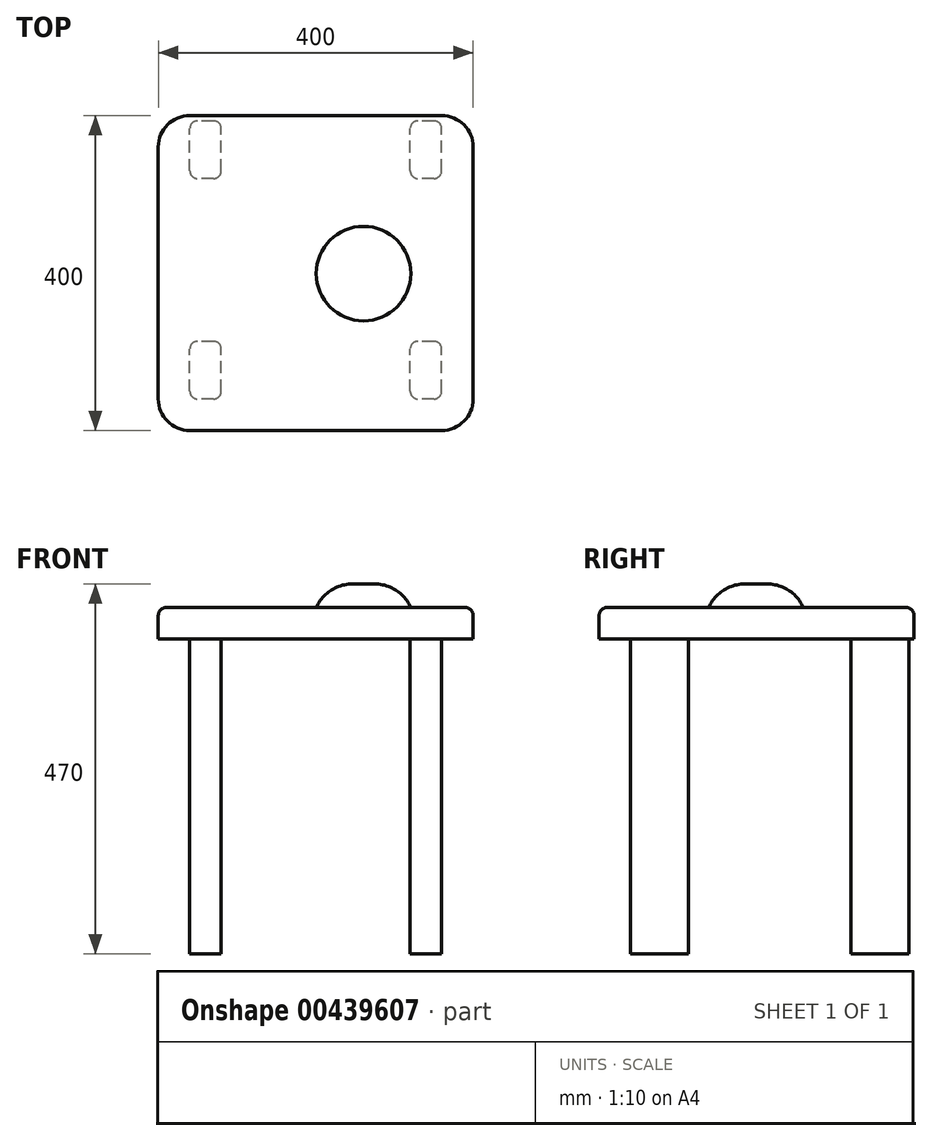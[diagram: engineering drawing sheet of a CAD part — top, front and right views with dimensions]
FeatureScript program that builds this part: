
annotation { "Feature Type Name" : "Feature", "Feature Type Description" : "" }
export const myFeature = defineFeature(function(context is Context, id is Id, definition is map)
    precondition{}
    {
        {
            var Q0;
            Q0=qCreatedBy(makeId("Top.planeOp"),FACE);
            var sketch = newSketch(context, id + "F0", { "sketchPlane" : qUnion([Q0])});
            skLineSegment(sketch, "E0.bottom", {"start": v(-220.7, -199.26) * mm, "end": v(99.3, -199.26) * mm});
            skLineSegment(sketch, "E0.top", {"start": v(-220.7, 200.74) * mm, "end": v(99.3, 200.74) * mm});
            skLineSegment(sketch, "E0.left", {"start": v(-260.7, -159.26) * mm, "end": v(-260.7, 160.74) * mm});
            skLineSegment(sketch, "E0.right", {"start": v(139.3, -159.26) * mm, "end": v(139.3, 160.74) * mm});
            skPoint(sketch, "E1.visualSharp", {"position": v(-260.7, 200.74) * mm});
            skArc(sketch, "E1.filletArc", {"start": v(-220.7, 200.74) * mm, "mid": v(-248.99, 189.03) * mm, "end": v(-260.7, 160.74) * mm});
            skPoint(sketch, "E2.visualSharp", {"position": v(139.3, 200.74) * mm});
            skArc(sketch, "E2.filletArc", {"start": v(139.3, 160.74) * mm, "mid": v(127.58, 189.03) * mm, "end": v(99.3, 200.74) * mm});
            skPoint(sketch, "E3.visualSharp", {"position": v(139.3, -199.26) * mm});
            skArc(sketch, "E3.filletArc", {"start": v(99.3, -199.26) * mm, "mid": v(127.58, -187.54) * mm, "end": v(139.3, -159.26) * mm});
            skPoint(sketch, "E4.visualSharp", {"position": v(-260.7, -199.26) * mm});
            skArc(sketch, "E4.filletArc", {"start": v(-260.7, -159.26) * mm, "mid": v(-248.99, -187.54) * mm, "end": v(-220.7, -199.26) * mm});
            skSolve(sketch);
        }
        {
            var Q0;
            Q0 = qSketchRegion(id + "F0", true);
            extrude(context, id + "F1", {"entities" : qUnion([Q0]), "depth" : 40 * mm});
        }
        {
            var Q0;
            Q0=makeQuery(id+"F1.opExtrude","CAP_FACE",FACE,{"disambiguationData":[OSD([sQuery(id+"F0.wireOp",EDGE,"E0.bottom"),sQuery(id+"F0.wireOp",EDGE,"E0.top"),sQuery(id+"F0.wireOp",EDGE,"E0.left"),sQuery(id+"F0.wireOp",EDGE,"E0.right"),sQuery(id+"F0.wireOp",EDGE,"E1.filletArc"),sQuery(id+"F0.wireOp",EDGE,"E2.filletArc"),sQuery(id+"F0.wireOp",EDGE,"E3.filletArc"),sQuery(id+"F0.wireOp",EDGE,"E4.filletArc")])],"isStart":false});
            fillet(context, id + "F2", {"entities" : qUnion([Q0]), "radius" : 10 * mm, "tangentPropagation" : true, "allowEdgeOverflow" : false});
        }
        {
            var Q0;
            Q0=makeQuery(id+"F1.opExtrude","CAP_FACE",FACE,{"disambiguationData":[OSD([sQuery(id+"F0.wireOp",EDGE,"E0.bottom"),sQuery(id+"F0.wireOp",EDGE,"E0.top"),sQuery(id+"F0.wireOp",EDGE,"E0.left"),sQuery(id+"F0.wireOp",EDGE,"E0.right"),sQuery(id+"F0.wireOp",EDGE,"E1.filletArc"),sQuery(id+"F0.wireOp",EDGE,"E2.filletArc"),sQuery(id+"F0.wireOp",EDGE,"E3.filletArc"),sQuery(id+"F0.wireOp",EDGE,"E4.filletArc")])],"isStart":true});
            var sketch = newSketch(context, id + "F3", { "sketchPlane" : qUnion([Q0])});
            skLineSegment(sketch, "E5.bottom", {"start": v(89.3, 159.26) * mm, "end": v(69.3, 159.26) * mm});
            skLineSegment(sketch, "E5.top", {"start": v(89.3, 86) * mm, "end": v(69.3, 86) * mm});
            skLineSegment(sketch, "E5.left", {"start": v(99.3, 149.26) * mm, "end": v(99.3, 96) * mm});
            skLineSegment(sketch, "E5.right", {"start": v(59.3, 149.26) * mm, "end": v(59.3, 96) * mm});
            skPoint(sketch, "E6.visualSharp", {"position": v(99.3, 159.26) * mm});
            skArc(sketch, "E6.filletArc", {"start": v(99.3, 149.26) * mm, "mid": v(96.37, 156.33) * mm, "end": v(89.3, 159.26) * mm});
            skPoint(sketch, "E7.visualSharp", {"position": v(99.3, 86) * mm});
            skArc(sketch, "E7.filletArc", {"start": v(89.3, 86) * mm, "mid": v(96.37, 88.93) * mm, "end": v(99.3, 96) * mm});
            skPoint(sketch, "E8.visualSharp", {"position": v(59.3, 86) * mm});
            skArc(sketch, "E8.filletArc", {"start": v(59.3, 96) * mm, "mid": v(62.22, 88.93) * mm, "end": v(69.3, 86) * mm});
            skPoint(sketch, "E9.visualSharp", {"position": v(59.3, 159.26) * mm});
            skArc(sketch, "E9.filletArc", {"start": v(69.3, 159.26) * mm, "mid": v(62.22, 156.33) * mm, "end": v(59.3, 149.26) * mm});
            skPoint(sketch, "E10.0.1.0", {"position": v(99.3, -194) * mm});
            skPoint(sketch, "E10.0.1.1", {"position": v(59.3, -120.74) * mm});
            skLineSegment(sketch, "E10.0.1.2", {"start": v(99.3, -130.74) * mm, "end": v(99.3, -184) * mm});
            skPoint(sketch, "E10.0.1.3", {"position": v(99.3, -120.74) * mm});
            skLineSegment(sketch, "E10.0.1.4", {"start": v(89.3, -194) * mm, "end": v(69.3, -194) * mm});
            skPoint(sketch, "E10.0.1.5", {"position": v(59.3, -194) * mm});
            skLineSegment(sketch, "E10.0.1.6", {"start": v(59.3, -130.74) * mm, "end": v(59.3, -184) * mm});
            skArc(sketch, "E10.0.1.7", {"start": v(59.3, -184) * mm, "mid": v(62.22, -191.07) * mm, "end": v(69.3, -194) * mm});
            skArc(sketch, "E10.0.1.8", {"start": v(69.3, -120.74) * mm, "mid": v(62.22, -123.67) * mm, "end": v(59.3, -130.74) * mm});
            skArc(sketch, "E10.0.1.9", {"start": v(99.3, -130.74) * mm, "mid": v(96.37, -123.67) * mm, "end": v(89.3, -120.74) * mm});
            skArc(sketch, "E10.0.1.10", {"start": v(89.3, -194) * mm, "mid": v(96.37, -191.07) * mm, "end": v(99.3, -184) * mm});
            skLineSegment(sketch, "E10.0.1.11", {"start": v(89.3, -120.74) * mm, "end": v(69.3, -120.74) * mm});
            skPoint(sketch, "E10.1.0.0", {"position": v(-180.7, 86) * mm});
            skPoint(sketch, "E10.1.0.1", {"position": v(-220.7, 159.26) * mm});
            skLineSegment(sketch, "E10.1.0.2", {"start": v(-180.7, 149.26) * mm, "end": v(-180.7, 96) * mm});
            skPoint(sketch, "E10.1.0.3", {"position": v(-180.7, 159.26) * mm});
            skLineSegment(sketch, "E10.1.0.4", {"start": v(-190.7, 86) * mm, "end": v(-210.7, 86) * mm});
            skPoint(sketch, "E10.1.0.5", {"position": v(-220.7, 86) * mm});
            skLineSegment(sketch, "E10.1.0.6", {"start": v(-220.7, 149.26) * mm, "end": v(-220.7, 96) * mm});
            skArc(sketch, "E10.1.0.7", {"start": v(-220.7, 96) * mm, "mid": v(-217.78, 88.93) * mm, "end": v(-210.7, 86) * mm});
            skArc(sketch, "E10.1.0.8", {"start": v(-210.7, 159.26) * mm, "mid": v(-217.78, 156.33) * mm, "end": v(-220.7, 149.26) * mm});
            skArc(sketch, "E10.1.0.9", {"start": v(-180.7, 149.26) * mm, "mid": v(-183.63, 156.33) * mm, "end": v(-190.7, 159.26) * mm});
            skArc(sketch, "E10.1.0.10", {"start": v(-190.7, 86) * mm, "mid": v(-183.63, 88.93) * mm, "end": v(-180.7, 96) * mm});
            skLineSegment(sketch, "E10.1.0.11", {"start": v(-190.7, 159.26) * mm, "end": v(-210.7, 159.26) * mm});
            skPoint(sketch, "E10.1.1.0", {"position": v(-180.7, -194) * mm});
            skPoint(sketch, "E10.1.1.1", {"position": v(-220.7, -120.74) * mm});
            skLineSegment(sketch, "E10.1.1.2", {"start": v(-180.7, -130.74) * mm, "end": v(-180.7, -184) * mm});
            skPoint(sketch, "E10.1.1.3", {"position": v(-180.7, -120.74) * mm});
            skLineSegment(sketch, "E10.1.1.4", {"start": v(-190.7, -194) * mm, "end": v(-210.7, -194) * mm});
            skPoint(sketch, "E10.1.1.5", {"position": v(-220.7, -194) * mm});
            skLineSegment(sketch, "E10.1.1.6", {"start": v(-220.7, -130.74) * mm, "end": v(-220.7, -184) * mm});
            skArc(sketch, "E10.1.1.7", {"start": v(-220.7, -184) * mm, "mid": v(-217.78, -191.07) * mm, "end": v(-210.7, -194) * mm});
            skArc(sketch, "E10.1.1.8", {"start": v(-210.7, -120.74) * mm, "mid": v(-217.78, -123.67) * mm, "end": v(-220.7, -130.74) * mm});
            skArc(sketch, "E10.1.1.9", {"start": v(-180.7, -130.74) * mm, "mid": v(-183.63, -123.67) * mm, "end": v(-190.7, -120.74) * mm});
            skArc(sketch, "E10.1.1.10", {"start": v(-190.7, -194) * mm, "mid": v(-183.63, -191.07) * mm, "end": v(-180.7, -184) * mm});
            skLineSegment(sketch, "E10.1.1.11", {"start": v(-190.7, -120.74) * mm, "end": v(-210.7, -120.74) * mm});
            skLineSegment(sketch, "E10.direction1", {"start": v(59.3, 86) * mm, "end": v(-220.7, 86) * mm, "construction": true});
            skLineSegment(sketch, "E10.direction2", {"start": v(59.3, 86) * mm, "end": v(59.3, -194) * mm, "construction": true});
            skSolve(sketch);
        }
        {
            var Q0;
            Q0=makeQuery(id+"F3.imprint","IMPRINT",FACE,{"disambiguationData":[TD([[makeQuery(id+"F3.imprint","IMPRINT",EDGE,{"derivedFrom":sQuery(id+"F3.wireOp",EDGE,"E10.0.1.2")}),-1.0]])]});
            var Q1;
            Q1=makeQuery(id+"F3.imprint","IMPRINT",FACE,{"disambiguationData":[TD([[makeQuery(id+"F3.imprint","IMPRINT",EDGE,{"derivedFrom":sQuery(id+"F3.wireOp",EDGE,"E5.bottom")}),1.0]])]});
            var Q2;
            Q2=makeQuery(id+"F3.imprint","IMPRINT",FACE,{"disambiguationData":[TD([[makeQuery(id+"F3.imprint","IMPRINT",EDGE,{"derivedFrom":sQuery(id+"F3.wireOp",EDGE,"E10.1.0.2")}),-1.0]])]});
            var Q3;
            Q3=makeQuery(id+"F3.imprint","IMPRINT",FACE,{"disambiguationData":[TD([[makeQuery(id+"F3.imprint","IMPRINT",EDGE,{"derivedFrom":sQuery(id+"F3.wireOp",EDGE,"E10.1.1.2")}),-1.0]])]});
            extrude(context, id + "F4", {"entities" : qUnion([Q0, Q1, Q2, Q3]), "operationType" : NewBodyOperationType.ADD, "depth" : 400 * mm});
        }
        {
            var Q0;
            Q0=makeQuery(id+"F1.opExtrude","CAP_FACE",FACE,{"disambiguationData":[OSD([sQuery(id+"F0.wireOp",EDGE,"E0.bottom"),sQuery(id+"F0.wireOp",EDGE,"E0.top"),sQuery(id+"F0.wireOp",EDGE,"E0.left"),sQuery(id+"F0.wireOp",EDGE,"E0.right"),sQuery(id+"F0.wireOp",EDGE,"E1.filletArc"),sQuery(id+"F0.wireOp",EDGE,"E2.filletArc"),sQuery(id+"F0.wireOp",EDGE,"E3.filletArc"),sQuery(id+"F0.wireOp",EDGE,"E4.filletArc")])],"isStart":false});
            var sketch = newSketch(context, id + "F5", { "sketchPlane" : qUnion([Q0])});
            skCircle(sketch, "E11", {"center": v(0, 0) * mm, "radius": 60.04 * mm});
            skSolve(sketch);
        }
        {
            var Q0;
            Q0=makeQuery(id+"F5.imprint","IMPRINT",FACE,{"disambiguationData":[TD([[makeQuery(id+"F5.imprint","IMPRINT",EDGE,{"derivedFrom":sQuery(id+"F5.wireOp",EDGE,"E11")}),1.0]])]});
            extrude(context, id + "F6", {"entities" : qUnion([Q0]), "operationType" : NewBodyOperationType.ADD, "depth" : 30 * mm});
        }
        {
            var Q0;
            Q0=makeQuery(id+"F6.opExtrude","CAP_EDGE",EDGE,{"disambiguationData":[OSD([sQuery(id+"F5.wireOp",EDGE,"E11")])],"isStart":false});
            fillet(context, id + "F7", {"entities" : qUnion([Q0]), "radius" : 50 * mm, "tangentPropagation" : true, "allowEdgeOverflow" : false});
        }
    });
